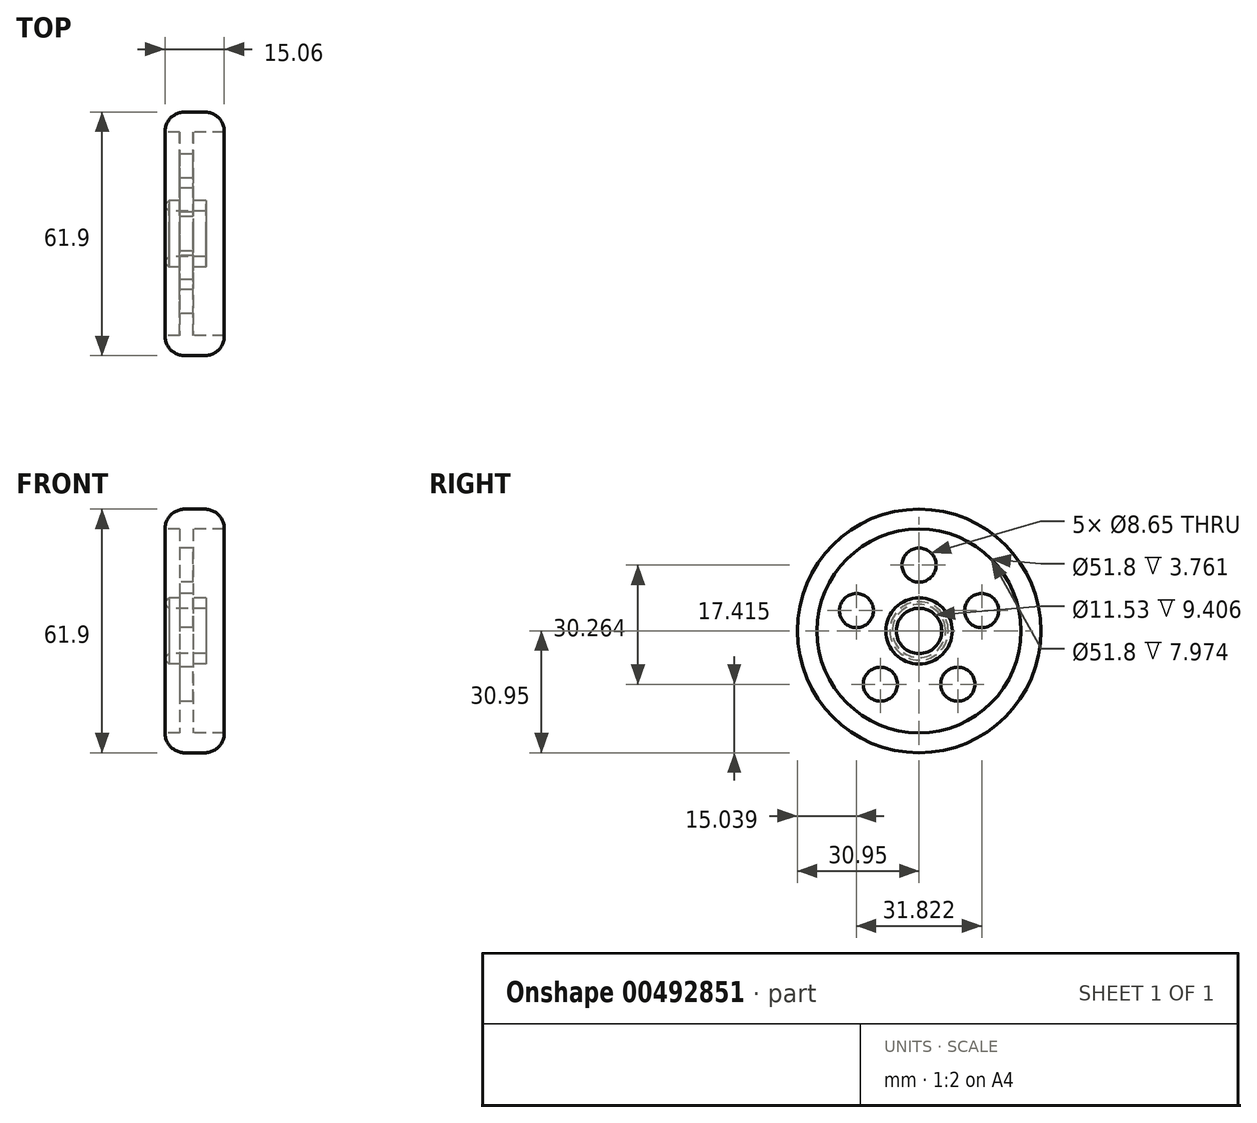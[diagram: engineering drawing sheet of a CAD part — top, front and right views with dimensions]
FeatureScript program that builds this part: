
annotation { "Feature Type Name" : "Feature", "Feature Type Description" : "" }
export const myFeature = defineFeature(function(context is Context, id is Id, definition is map)
    precondition{}
    {
        {
            var Q0;
            Q0=qCreatedBy(makeId("Front.planeOp"),FACE);
            var sketch = newSketch(context, id + "F0", { "sketchPlane" : qUnion([Q0])});
            skLineSegment(sketch, "E0", {"start": v(0, 30.95) * mm, "end": v(15.06, 30.95) * mm});
            skLineSegment(sketch, "E1", {"start": v(15.06, 30.95) * mm, "end": v(15.06, 25.9) * mm});
            skLineSegment(sketch, "E2", {"start": v(15.06, 25.9) * mm, "end": v(7.08, 25.9) * mm});
            skLineSegment(sketch, "E3", {"start": v(7.08, 25.9) * mm, "end": v(7.08, 8.43) * mm});
            skLineSegment(sketch, "E4", {"start": v(7.08, 8.43) * mm, "end": v(10.4, 8.43) * mm});
            skLineSegment(sketch, "E5", {"start": v(10.4, 8.43) * mm, "end": v(10.4, 5.77) * mm});
            skLineSegment(sketch, "E6", {"start": v(10.4, 5.77) * mm, "end": v(0, 5.77) * mm});
            skLineSegment(sketch, "E7", {"start": v(0, 5.77) * mm, "end": v(0, 8.43) * mm});
            skLineSegment(sketch, "E8", {"start": v(0, 8.43) * mm, "end": v(3.76, 8.43) * mm});
            skLineSegment(sketch, "E9", {"start": v(3.76, 8.43) * mm, "end": v(3.76, 25.9) * mm});
            skLineSegment(sketch, "E10", {"start": v(3.76, 25.9) * mm, "end": v(0, 25.9) * mm});
            skLineSegment(sketch, "E11", {"start": v(0, 25.9) * mm, "end": v(0, 30.95) * mm});
            skLineSegment(sketch, "E12", {"start": v(0, 0) * mm, "end": v(10.4, 0) * mm});
            skSolve(sketch);
        }
        {
            var Q0;
            Q0 = qSketchRegion(id + "F0", true);
            var Q1;
            Q1=sQuery(id+"F0.wireOp",EDGE,"E12");
            revolve(context, id + "F1", {"entities" : qUnion([Q0]), "axis" : qUnion([Q1]), "revolveType" : RevolveType.FULL});
        }
        {
            var Q0;
            Q0=makeQuery(id+"F1.opRevolve","SWEPT_FACE",FACE,{"disambiguationData":[OSD([sQuery(id+"F0.wireOp",EDGE,"E9")])]});
            var sketch = newSketch(context, id + "F2", { "sketchPlane" : qUnion([Q0])});
            skCircle(sketch, "E13", {"center": v(0, 16.73) * mm, "radius": 4.24 * mm});
            skCircle(sketch, "E14.1.0", {"center": v(-15.91, 5.17) * mm, "radius": 4.24 * mm});
            skCircle(sketch, "E14.2.0", {"center": v(-9.83, -13.53) * mm, "radius": 4.24 * mm});
            skCircle(sketch, "E14.3.0", {"center": v(9.83, -13.53) * mm, "radius": 4.24 * mm});
            skCircle(sketch, "E14.4.0", {"center": v(15.91, 5.17) * mm, "radius": 4.24 * mm});
            skPoint(sketch, "E14.center", {"position": v(0, 0) * mm});
            skSolve(sketch);
        }
        {
            var Q0;
            Q0=sQuery(id+"F2.wireOp",VERTEX,"E14.1.0.center");
            var Q1;
            Q1=sQuery(id+"F2.wireOp",VERTEX,"E13.center");
            var Q2;
            Q2=sQuery(id+"F2.wireOp",VERTEX,"E14.4.0.center");
            var Q3;
            Q3=sQuery(id+"F2.wireOp",VERTEX,"E14.3.0.center");
            var Q4;
            Q4=sQuery(id+"F2.wireOp",VERTEX,"E14.2.0.center");
            var Q5;
            Q5=makeQuery(id+"F1.opRevolve","SWEPT_BODY",BODY,{"disambiguationData":[OSD([sQuery(id+"F0.wireOp",EDGE,"E0"),sQuery(id+"F0.wireOp",EDGE,"E1"),sQuery(id+"F0.wireOp",EDGE,"E2"),sQuery(id+"F0.wireOp",EDGE,"E3"),sQuery(id+"F0.wireOp",EDGE,"E4"),sQuery(id+"F0.wireOp",EDGE,"E5"),sQuery(id+"F0.wireOp",EDGE,"E6"),sQuery(id+"F0.wireOp",EDGE,"E7"),sQuery(id+"F0.wireOp",EDGE,"E8"),sQuery(id+"F0.wireOp",EDGE,"E9"),sQuery(id+"F0.wireOp",EDGE,"E10"),sQuery(id+"F0.wireOp",EDGE,"E11")])]});
            hole(context, id + "F3", {"style" : HoleStyle.SIMPLE, "endStyle" : HoleEndStyle.BLIND, "holeDiameter" : 8.65 * mm, "holeDepth" : 10 * mm, "isTappedThrough" : true, "tappedDepth" : 12.7 * mm, "tapClearance" : 3, "locations" : qUnion([Q0, Q1, Q2, Q3, Q4]), "scope" : qUnion([Q5])});
        }
        {
            var Q0;
            Q0=makeQuery(id+"F1.opRevolve","SWEPT_EDGE",EDGE,{"disambiguationData":[OSD([sQuery(id+"F0.wireOp",EDGE,"E0"),sQuery(id+"F0.wireOp",EDGE,"E11")])]});
            var Q1;
            Q1=makeQuery(id+"F1.opRevolve","SWEPT_EDGE",EDGE,{"disambiguationData":[OSD([sQuery(id+"F0.wireOp",EDGE,"E0"),sQuery(id+"F0.wireOp",EDGE,"E1")])]});
            fillet(context, id + "F4", {"entities" : qUnion([Q0, Q1]), "radius" : 5 * mm, "tangentPropagation" : true, "allowEdgeOverflow" : false});
        }
        {
            var Q0;
            Q0=makeQuery(id+"F3.hole-0.boolean.opBoolean","COPY",EDGE,{"derivedFrom":makeQuery(id+"F3.hole-0.opRevolve","SWEPT_EDGE",EDGE,{"disambiguationData":[OSD([sQuery(id+"F3.hole-0.sketch.wireOp",EDGE,"core_line_2"),sQuery(id+"F3.hole-0.sketch.wireOp",EDGE,"core_line_3")])]})});
            var Q1;
            Q1=makeQuery(id+"F3.hole-4.boolean.opBoolean","INTERSECT",EDGE,{"derivedFrom":[makeQuery(id+"F1.opRevolve","SWEPT_FACE",FACE,{"disambiguationData":[OSD([sQuery(id+"F0.wireOp",EDGE,"E3")])]}),makeQuery(id+"F3.hole-4.opRevolve","SWEPT_FACE",FACE,{"disambiguationData":[OSD([sQuery(id+"F3.hole-4.sketch.wireOp",EDGE,"core_line_2")])]})]});
            var Q2;
            Q2=makeQuery(id+"F3.hole-4.boolean.opBoolean","COPY",EDGE,{"derivedFrom":makeQuery(id+"F3.hole-4.opRevolve","SWEPT_EDGE",EDGE,{"disambiguationData":[OSD([sQuery(id+"F3.hole-4.sketch.wireOp",EDGE,"core_line_2"),sQuery(id+"F3.hole-4.sketch.wireOp",EDGE,"core_line_3")])]})});
            var Q3;
            Q3=makeQuery(id+"F3.hole-3.boolean.opBoolean","INTERSECT",EDGE,{"derivedFrom":[makeQuery(id+"F1.opRevolve","SWEPT_FACE",FACE,{"disambiguationData":[OSD([sQuery(id+"F0.wireOp",EDGE,"E3")])]}),makeQuery(id+"F3.hole-3.opRevolve","SWEPT_FACE",FACE,{"disambiguationData":[OSD([sQuery(id+"F3.hole-3.sketch.wireOp",EDGE,"core_line_2")])]})]});
            var Q4;
            Q4=makeQuery(id+"F3.hole-3.boolean.opBoolean","COPY",EDGE,{"derivedFrom":makeQuery(id+"F3.hole-3.opRevolve","SWEPT_EDGE",EDGE,{"disambiguationData":[OSD([sQuery(id+"F3.hole-3.sketch.wireOp",EDGE,"core_line_2"),sQuery(id+"F3.hole-3.sketch.wireOp",EDGE,"core_line_3")])]})});
            var Q5;
            Q5=makeQuery(id+"F3.hole-2.boolean.opBoolean","COPY",EDGE,{"derivedFrom":makeQuery(id+"F3.hole-2.opRevolve","SWEPT_EDGE",EDGE,{"disambiguationData":[OSD([sQuery(id+"F3.hole-2.sketch.wireOp",EDGE,"core_line_2"),sQuery(id+"F3.hole-2.sketch.wireOp",EDGE,"core_line_3")])]})});
            var Q6;
            Q6=makeQuery(id+"F3.hole-2.boolean.opBoolean","INTERSECT",EDGE,{"derivedFrom":[makeQuery(id+"F1.opRevolve","SWEPT_FACE",FACE,{"disambiguationData":[OSD([sQuery(id+"F0.wireOp",EDGE,"E3")])]}),makeQuery(id+"F3.hole-2.opRevolve","SWEPT_FACE",FACE,{"disambiguationData":[OSD([sQuery(id+"F3.hole-2.sketch.wireOp",EDGE,"core_line_2")])]})]});
            var Q7;
            Q7=makeQuery(id+"F3.hole-1.boolean.opBoolean","COPY",EDGE,{"derivedFrom":makeQuery(id+"F3.hole-1.opRevolve","SWEPT_EDGE",EDGE,{"disambiguationData":[OSD([sQuery(id+"F3.hole-1.sketch.wireOp",EDGE,"core_line_2"),sQuery(id+"F3.hole-1.sketch.wireOp",EDGE,"core_line_3")])]})});
            var Q8;
            Q8=makeQuery(id+"F3.hole-1.boolean.opBoolean","INTERSECT",EDGE,{"derivedFrom":[makeQuery(id+"F1.opRevolve","SWEPT_FACE",FACE,{"disambiguationData":[OSD([sQuery(id+"F0.wireOp",EDGE,"E3")])]}),makeQuery(id+"F3.hole-1.opRevolve","SWEPT_FACE",FACE,{"disambiguationData":[OSD([sQuery(id+"F3.hole-1.sketch.wireOp",EDGE,"core_line_2")])]})]});
            var Q9;
            Q9=makeQuery(id+"F1.opRevolve","SWEPT_EDGE",EDGE,{"disambiguationData":[OSD([sQuery(id+"F0.wireOp",EDGE,"E7"),sQuery(id+"F0.wireOp",EDGE,"E8")])]});
            var Q10;
            Q10=makeQuery(id+"F1.opRevolve","SWEPT_EDGE",EDGE,{"disambiguationData":[OSD([sQuery(id+"F0.wireOp",EDGE,"E6"),sQuery(id+"F0.wireOp",EDGE,"E7")])]});
            chamfer(context, id + "F5", {"entities" : qUnion([Q0, Q1, Q2, Q3, Q4, Q5, Q6, Q7, Q8, Q9, Q10]), "width" : 1 * mm, "tangentPropagation" : true});
        }
    });
